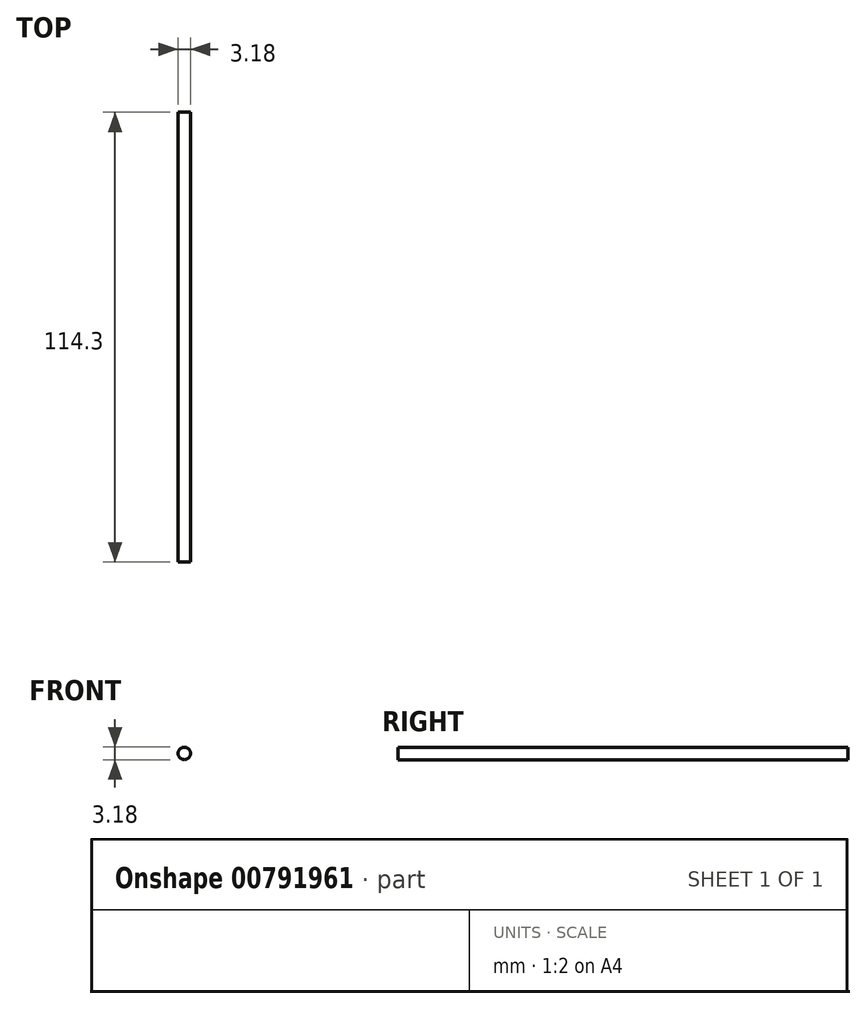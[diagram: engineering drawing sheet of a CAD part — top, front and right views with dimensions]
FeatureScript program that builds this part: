
annotation { "Feature Type Name" : "Feature", "Feature Type Description" : "" }
export const myFeature = defineFeature(function(context is Context, id is Id, definition is map)
    precondition{}
    {
        {
            var Q0;
            Q0=qCreatedBy(makeId("Front.planeOp"),FACE);
            var sketch = newSketch(context, id + "F0", { "sketchPlane" : qUnion([Q0])});
            skCircle(sketch, "E0", {"center": v(0, 0) * mm, "radius": 1.59 * mm});
            skSolve(sketch);
        }
        {
            var Q0;
            Q0=makeQuery(id+"F0.imprint","IMPRINT",FACE,{"disambiguationData":[TD([[makeQuery(id+"F0.imprint","IMPRINT",EDGE,{"derivedFrom":sQuery(id+"F0.wireOp",EDGE,"E0")}),1.0]])]});
            var Q1;
            Q1=sQuery(id+"F0.wireOp",EDGE,"E0");
            extrude(context, id + "F1", {"entities" : qUnion([Q0]), "surfaceEntities" : qUnion([Q1]), "depth" : 114.3 * mm, "offsetDistance" : 25.4 * mm});
        }
    });
